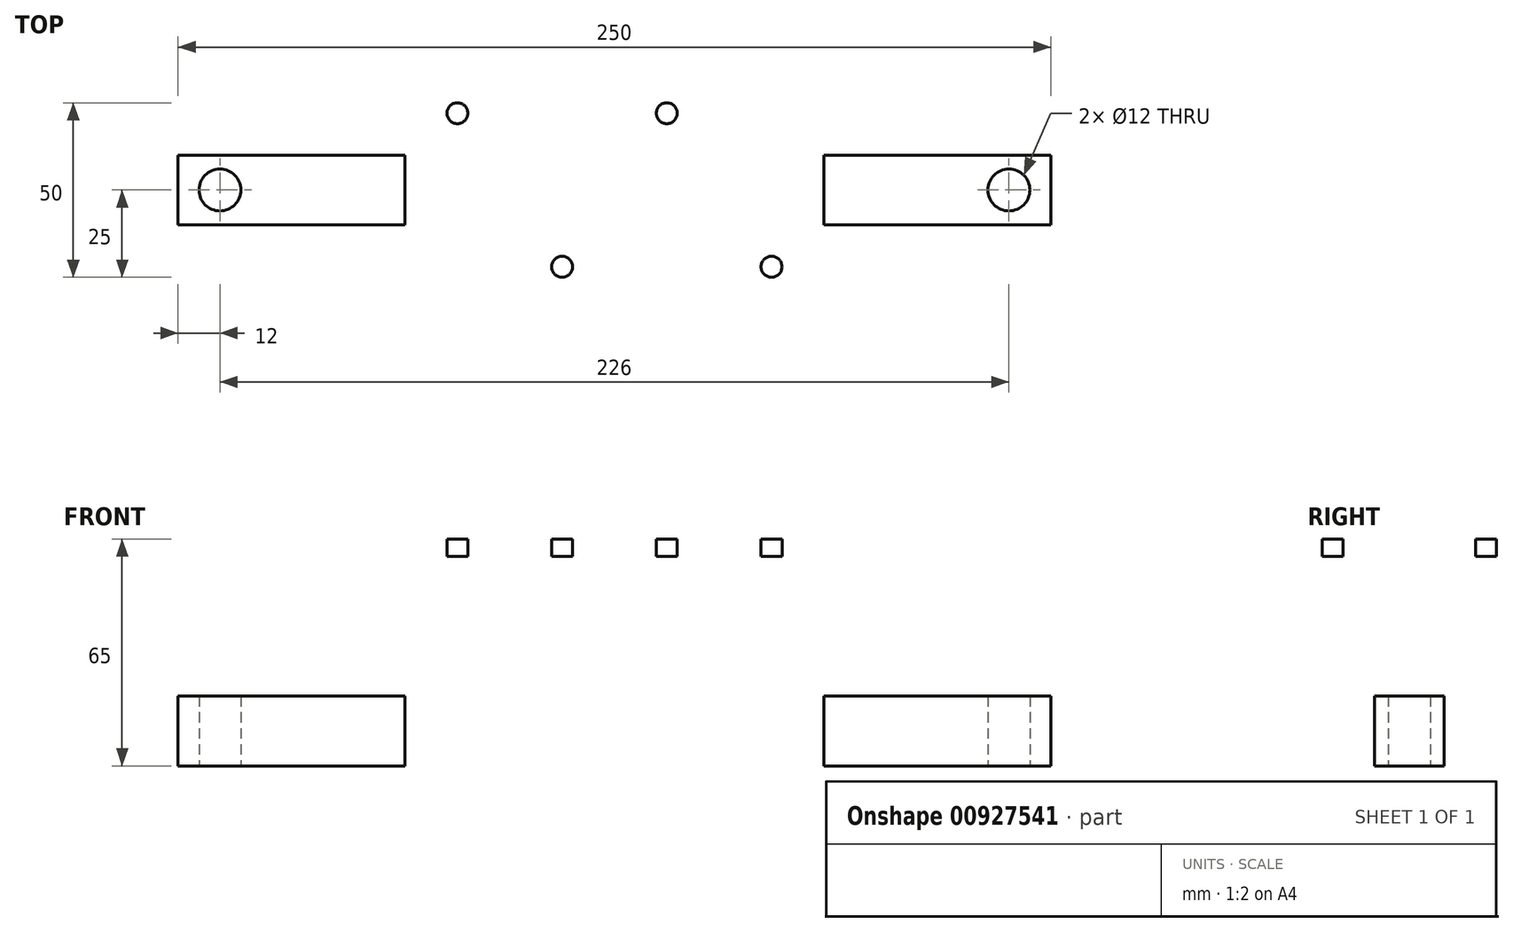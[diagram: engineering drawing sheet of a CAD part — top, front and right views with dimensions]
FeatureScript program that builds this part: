
annotation { "Feature Type Name" : "Feature", "Feature Type Description" : "" }
export const myFeature = defineFeature(function(context is Context, id is Id, definition is map)
    precondition{}
    {
        {
            var Q0;
            Q0=qCreatedBy(makeId("Top.planeOp"),FACE);
            var sketch = newSketch(context, id + "F0", { "sketchPlane" : qUnion([Q0])});
            skLineSegment(sketch, "E0.bottom", {"start": v(60, -30) * mm, "end": v(-60, -30) * mm});
            skLineSegment(sketch, "E0.top", {"start": v(60, 30) * mm, "end": v(-60, 30) * mm});
            skLineSegment(sketch, "E0.left", {"start": v(60, -30) * mm, "end": v(60, 30) * mm});
            skLineSegment(sketch, "E0.right", {"start": v(-60, -30) * mm, "end": v(-60, 30) * mm});
            skPoint(sketch, "E0.middle", {"position": v(0, 0) * mm});
            skLineSegment(sketch, "E1", {"start": v(-54.33, 0) * mm, "end": v(81.26, 0) * mm, "construction": true});
            skSolve(sketch);
        }
        {
            var Q0;
            Q0 = qSketchRegion(id + "F0", true);
            extrude(context, id + "F1", {"entities" : qUnion([Q0]), "depth" : 5 * mm, "offsetDistance" : 25 * mm});
        }
        {
            var Q0;
            Q0=makeQuery(id+"F1.opExtrude","CAP_FACE",FACE,{"disambiguationData":[OSD([sQuery(id+"F0.wireOp",EDGE,"E0.bottom"),sQuery(id+"F0.wireOp",EDGE,"E0.top"),sQuery(id+"F0.wireOp",EDGE,"E0.left"),sQuery(id+"F0.wireOp",EDGE,"E0.right")])],"isStart":true});
            var sketch = newSketch(context, id + "F2", { "sketchPlane" : qUnion([Q0])});
            skLineSegment(sketch, "E2.bottom", {"start": v(20, -10) * mm, "end": v(-20, -10) * mm});
            skLineSegment(sketch, "E2.top", {"start": v(20, 10) * mm, "end": v(-20, 10) * mm});
            skLineSegment(sketch, "E2.left", {"start": v(20, -10) * mm, "end": v(20, 10) * mm});
            skLineSegment(sketch, "E2.right", {"start": v(-20, -10) * mm, "end": v(-20, 10) * mm});
            skPoint(sketch, "E2.middle", {"position": v(0, 0) * mm});
            skSolve(sketch);
        }
        {
            var Q0;
            Q0 = qSketchRegion(id + "F2", true);
            extrude(context, id + "F3", {"entities" : qUnion([Q0]), "operationType" : NewBodyOperationType.ADD, "depth" : 40 * mm, "offsetDistance" : 25 * mm});
        }
        {
            var Q0;
            Q0=makeQuery(id+"F3.opExtrude","CAP_FACE",FACE,{"disambiguationData":[OSD([sQuery(id+"F2.wireOp",EDGE,"E2.bottom"),sQuery(id+"F2.wireOp",EDGE,"E2.top"),sQuery(id+"F2.wireOp",EDGE,"E2.left"),sQuery(id+"F2.wireOp",EDGE,"E2.right")])],"isStart":false});
            var sketch = newSketch(context, id + "F4", { "sketchPlane" : qUnion([Q0])});
            skLineSegment(sketch, "E3.bottom", {"start": v(125, -10) * mm, "end": v(-125, -10) * mm});
            skLineSegment(sketch, "E3.top", {"start": v(125, 10) * mm, "end": v(-125, 10) * mm});
            skLineSegment(sketch, "E3.left", {"start": v(125, -10) * mm, "end": v(125, 10) * mm});
            skLineSegment(sketch, "E3.right", {"start": v(-125, -10) * mm, "end": v(-125, 10) * mm});
            skPoint(sketch, "E3.middle", {"position": v(0, 0) * mm});
            skSolve(sketch);
        }
        {
            var Q0;
            Q0 = qSketchRegion(id + "F4", true);
            extrude(context, id + "F5", {"entities" : qUnion([Q0]), "operationType" : NewBodyOperationType.ADD, "depth" : 20 * mm, "offsetDistance" : 25 * mm});
        }
        {
            var Q0;
            Q0=makeQuery(id+"F3.opExtrude","CAP_EDGE",EDGE,{"disambiguationData":[OSD([sQuery(id+"F2.wireOp",EDGE,"E2.right")])],"isStart":false});
            var Q1;
            Q1=makeQuery(id+"F3.opExtrude","CAP_EDGE",EDGE,{"disambiguationData":[OSD([sQuery(id+"F2.wireOp",EDGE,"E2.left")])],"isStart":false});
            var Q2;
            Q2=makeQuery(id+"F3.opExtrude","CAP_EDGE",EDGE,{"disambiguationData":[OSD([sQuery(id+"F2.wireOp",EDGE,"E2.left")])],"isStart":true});
            var Q3;
            Q3=makeQuery(id+"F3.opExtrude","CAP_EDGE",EDGE,{"disambiguationData":[OSD([sQuery(id+"F2.wireOp",EDGE,"E2.right")])],"isStart":true});
            fillet(context, id + "F6", {"entities" : qUnion([Q0, Q1, Q2, Q3]), "radius" : 10 * mm, "tangentPropagation" : true, "allowEdgeOverflow" : false});
        }
        {
            var Q0;
            Q0=makeQuery(id+"F5.opExtrude","CAP_FACE",FACE,{"disambiguationData":[OSD([sQuery(id+"F4.wireOp",EDGE,"E3.bottom"),sQuery(id+"F4.wireOp",EDGE,"E3.top"),sQuery(id+"F4.wireOp",EDGE,"E3.left"),sQuery(id+"F4.wireOp",EDGE,"E3.right")])],"isStart":false});
            var sketch = newSketch(context, id + "F7", { "sketchPlane" : qUnion([Q0])});
            skLineSegment(sketch, "E4", {"start": v(-106.95, 0) * mm, "end": v(110.34, 0) * mm, "construction": true});
            skPoint(sketch, "E4.startSnap0", {"position": v(-125, 0) * mm});
            skCircle(sketch, "E5", {"center": v(-113, 0) * mm, "radius": 6 * mm});
            skCircle(sketch, "E6", {"center": v(113, 0) * mm, "radius": 6 * mm});
            skSolve(sketch);
        }
        {
            var Q0;
            Q0 = qSketchRegion(id + "F7", true);
            extrude(context, id + "F8", {"entities" : qUnion([Q0]), "operationType" : NewBodyOperationType.REMOVE, "endBound" : BoundingType.THROUGH_ALL, "oppositeDirection" : true, "depth" : 25 * mm, "offsetDistance" : 25 * mm});
        }
        {
            var Q0;
            Q0=makeQuery(id+"F1.opExtrude","CAP_FACE",FACE,{"disambiguationData":[OSD([sQuery(id+"F0.wireOp",EDGE,"E0.bottom"),sQuery(id+"F0.wireOp",EDGE,"E0.top"),sQuery(id+"F0.wireOp",EDGE,"E0.left"),sQuery(id+"F0.wireOp",EDGE,"E0.right")])],"isStart":false});
            var sketch = newSketch(context, id + "F9", { "sketchPlane" : qUnion([Q0])});
            skLineSegment(sketch, "E7", {"start": v(-15, 47.4) * mm, "end": v(-15, -41.36) * mm, "construction": true});
            skCircle(sketch, "E8", {"center": v(-15, 22) * mm, "radius": 3 * mm});
            skCircle(sketch, "E9.MirrorC", {"center": v(15, 22) * mm, "radius": 3 * mm});
            skCircle(sketch, "E10.MirrorC", {"center": v(15, -22) * mm, "radius": 3 * mm});
            skCircle(sketch, "E11.MirrorC", {"center": v(-15, -22) * mm, "radius": 3 * mm});
            skLineSegment(sketch, "E12", {"start": v(-30, 45.95) * mm, "end": v(-30, -45.19) * mm, "construction": true});
            skCircle(sketch, "E13.MirrorC", {"center": v(-45, 22) * mm, "radius": 3 * mm});
            skCircle(sketch, "E14.MirrorC", {"center": v(-45, -22) * mm, "radius": 3 * mm});
            skLineSegment(sketch, "E15.MirrorCS", {"start": v(30, 45.95) * mm, "end": v(30, -45.19) * mm, "construction": true});
            skCircle(sketch, "E16.MirrorC", {"center": v(45, 22) * mm, "radius": 3 * mm});
            skCircle(sketch, "E17.MirrorC", {"center": v(45, -22) * mm, "radius": 3 * mm});
            skSolve(sketch);
        }
        {
            var Q0;
            Q0=makeQuery(id+"F9.imprint","IMPRINT",FACE,{"disambiguationData":[TD([[makeQuery(id+"F9.imprint","IMPRINT",EDGE,{"derivedFrom":sQuery(id+"F9.wireOp",EDGE,"E8")}),1.0]])]});
            var Q1;
            Q1=makeQuery(id+"F9.imprint","IMPRINT",FACE,{"disambiguationData":[TD([[makeQuery(id+"F9.imprint","IMPRINT",EDGE,{"derivedFrom":sQuery(id+"F9.wireOp",EDGE,"E9.MirrorC")}),-1.0]])]});
            var Q2;
            Q2=makeQuery(id+"F9.imprint","IMPRINT",FACE,{"disambiguationData":[TD([[makeQuery(id+"F9.imprint","IMPRINT",EDGE,{"derivedFrom":sQuery(id+"F9.wireOp",EDGE,"E11.MirrorC")}),-1.0]])]});
            var Q3;
            Q3=makeQuery(id+"F9.imprint","IMPRINT",FACE,{"disambiguationData":[TD([[makeQuery(id+"F9.imprint","IMPRINT",EDGE,{"derivedFrom":sQuery(id+"F9.wireOp",EDGE,"E10.MirrorC")}),1.0]])]});
            var Q4;
            Q4=makeQuery(id+"F9.imprint","IMPRINT",FACE,{"disambiguationData":[TD([[makeQuery(id+"F9.imprint","IMPRINT",EDGE,{"derivedFrom":sQuery(id+"F9.wireOp",EDGE,"E13.MirrorC")}),-1.0]])]});
            var Q5;
            Q5=makeQuery(id+"F9.imprint","IMPRINT",FACE,{"disambiguationData":[TD([[makeQuery(id+"F9.imprint","IMPRINT",EDGE,{"derivedFrom":sQuery(id+"F9.wireOp",EDGE,"E14.MirrorC")}),1.0]])]});
            var Q6;
            Q6=makeQuery(id+"F9.imprint","IMPRINT",FACE,{"disambiguationData":[TD([[makeQuery(id+"F9.imprint","IMPRINT",EDGE,{"derivedFrom":sQuery(id+"F9.wireOp",EDGE,"E16.MirrorC")}),1.0]])]});
            var Q7;
            Q7=makeQuery(id+"F9.imprint","IMPRINT",FACE,{"disambiguationData":[TD([[makeQuery(id+"F9.imprint","IMPRINT",EDGE,{"derivedFrom":sQuery(id+"F9.wireOp",EDGE,"E17.MirrorC")}),-1.0]])]});
            extrude(context, id + "F10", {"entities" : qUnion([Q0, Q1, Q2, Q3, Q4, Q5, Q6, Q7]), "operationType" : NewBodyOperationType.REMOVE, "endBound" : BoundingType.THROUGH_ALL, "oppositeDirection" : true, "depth" : 25 * mm, "offsetDistance" : 25 * mm});
        }
    });
